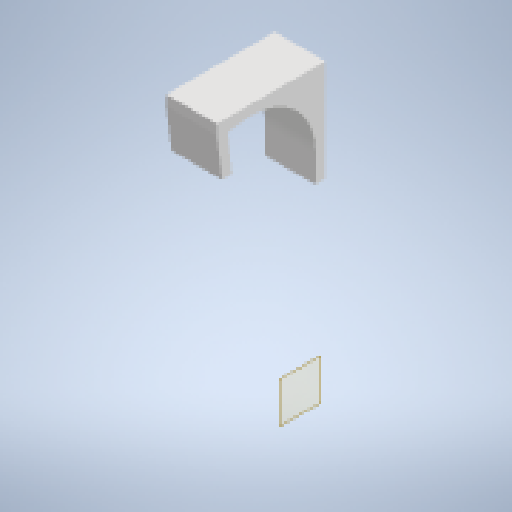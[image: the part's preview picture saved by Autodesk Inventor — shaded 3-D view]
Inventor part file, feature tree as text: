
AUTODESK INVENTOR PART (.ipt)
format: ipt  version: 2023 (Build 270158000, 158)  size: 164,352 bytes
history: native  units: mm
features: other x4, extrude x2, reference x2, plane x1, sketch x1, fillet x1
ambient origin geometry x8: Origin, YZ Plane, XZ Plane, XY Plane, X Axis, Y Axis, Z Axis, Center Point
bodies: Solid1 (feature_tree)
feature tree (11):
  plane  "Work Plane1"
  sketch  "Sketch2"  dims[d0=78.575mm d2=5.0mm d3=20.0mm d4=50.0mm d5=5.0mm d6=5.0mm d7=40.0mm d8=5.0mm d9=0.65mm d10=25.0mm d11=0.0mm d12=13.2mm d13=0.0mm d14=31.25mm]
  extrude  "Extrusion1"  Depth=5.0mm
  extrude  "Extrusion2"  Depth=20.0mm
  fillet  "Fillet1"  Radius=50.0mm
  reference  "Reference1"
  reference  "Reference2"
  parser-record x1  (decoder bookkeeping rows leaked as tree rows — omitted from the tree; the rows remain in map.json)
  other  "Assembly.iam"
  other  "Album:1"
  other  "wall:1"
note: 1 file-system path scrubbed to <path> (originals preserved in map.json)
